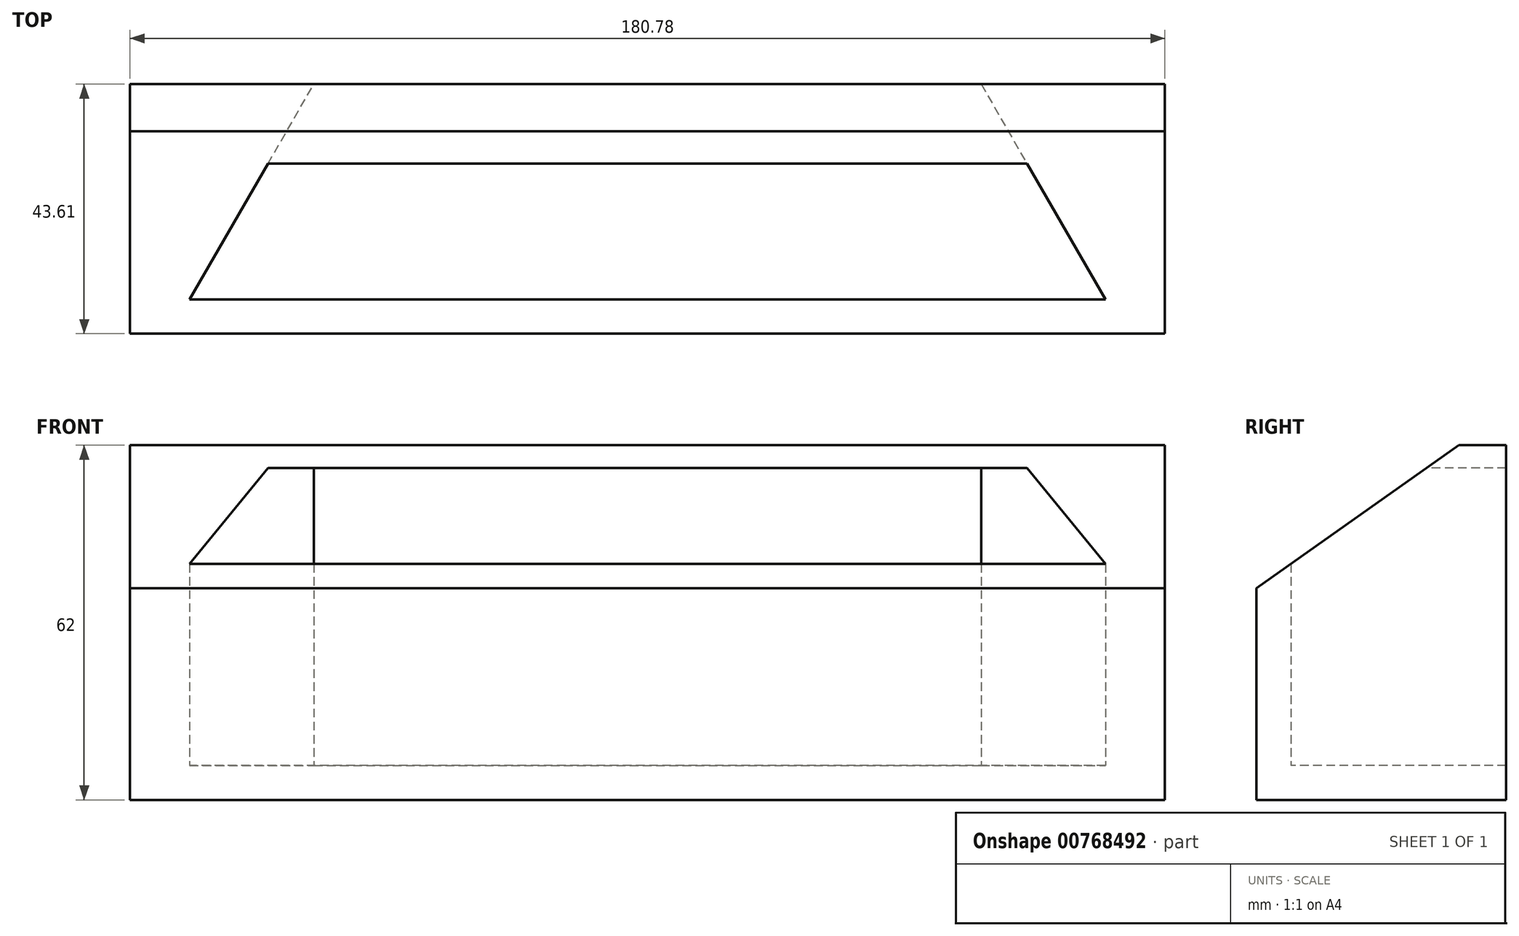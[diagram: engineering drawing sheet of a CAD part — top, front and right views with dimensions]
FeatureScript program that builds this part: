
annotation { "Feature Type Name" : "Feature", "Feature Type Description" : "" }
export const myFeature = defineFeature(function(context is Context, id is Id, definition is map)
    precondition{}
    {
        {
            var Q0;
            Q0=qCreatedBy(makeId("Top.planeOp"),FACE);
            var sketch = newSketch(context, id + "F0", { "sketchPlane" : qUnion([Q0])});
            skLineSegment(sketch, "E0.0", {"start": v(-80, -24) * mm, "end": v(0, 114.56) * mm});
            skLineSegment(sketch, "E0.1", {"start": v(0, 114.56) * mm, "end": v(80, -24) * mm});
            skLineSegment(sketch, "E0.2", {"start": v(80, -24) * mm, "end": v(-80, -24) * mm});
            skPoint(sketch, "E0.0.midPoint", {"position": v(-40, 45.28) * mm});
            skLineSegment(sketch, "E1", {"start": v(0, 126.56) * mm, "end": v(-90.4, -30) * mm});
            skLineSegment(sketch, "E2", {"start": v(-90.4, -30) * mm, "end": v(90.4, -30) * mm});
            skLineSegment(sketch, "E3", {"start": v(90.4, -30) * mm, "end": v(0, 126.56) * mm});
            skLineSegment(sketch, "E4", {"start": v(-90.4, -30) * mm, "end": v(-90.4, 0) * mm});
            skLineSegment(sketch, "E5", {"start": v(73.07, 0) * mm, "end": v(90.4, 0) * mm});
            skLineSegment(sketch, "E6", {"start": v(90.4, -30) * mm, "end": v(90.4, 0) * mm});
            skLineSegment(sketch, "E7", {"start": v(-90.4, 0) * mm, "end": v(-73.07, 0) * mm});
            skLineSegment(sketch, "E8", {"start": v(-58.29, 13.6) * mm, "end": v(58.29, 13.6) * mm});
            skLineSegment(sketch, "E9", {"start": v(-58.29, 13.6) * mm, "end": v(-65.21, 13.6) * mm});
            skLineSegment(sketch, "E10", {"start": v(58.29, 13.6) * mm, "end": v(65.21, 13.6) * mm});
            skLineSegment(sketch, "E11", {"start": v(-90.4, 0) * mm, "end": v(-90.4, 13.6) * mm});
            skLineSegment(sketch, "E12", {"start": v(-65.21, 13.6) * mm, "end": v(-90.4, 13.6) * mm});
            skLineSegment(sketch, "E13", {"start": v(90.4, 0) * mm, "end": v(90.4, 13.6) * mm});
            skLineSegment(sketch, "E14", {"start": v(65.21, 13.6) * mm, "end": v(90.4, 13.6) * mm});
            skLineSegment(sketch, "E15", {"start": v(-90.4, -30) * mm, "end": v(-90.4, -51.53) * mm});
            skLineSegment(sketch, "E16", {"start": v(-90.4, -51.53) * mm, "end": v(90.4, -51.53) * mm});
            skLineSegment(sketch, "E17", {"start": v(90.4, -30) * mm, "end": v(90.4, -51.53) * mm});
            skSolve(sketch);
        }
        {
            var Q0;
            {var subQ4=sQuery(id+"F0.wireOp",EDGE,"E0.2");Q0=makeQuery(id+"F0.imprint","IMPRINT",FACE,{"disambiguationData":[TD([[makeQuery(id+"F0.imprint","IMPRINT",EDGE,{"derivedFrom":subQ4}),1.0]])]});}
            var Q1;
            {var subQ0=sQuery(id+"F0.wireOp",EDGE,"E4");Q1=makeQuery(id+"F0.imprint","IMPRINT",FACE,{"disambiguationData":[TD([[makeQuery(id+"F0.imprint","IMPRINT",EDGE,{"derivedFrom":subQ0}),-1.0]])]});}
            var Q2;
            {var subQ0=sQuery(id+"F0.wireOp",EDGE,"E6");Q2=makeQuery(id+"F0.imprint","IMPRINT",FACE,{"disambiguationData":[TD([[makeQuery(id+"F0.imprint","IMPRINT",EDGE,{"derivedFrom":subQ0}),1.0]])]});}
            var Q3;
            {var subQ0=sQuery(id+"F0.wireOp",EDGE,"E7");Q3=makeQuery(id+"F0.imprint","IMPRINT",FACE,{"disambiguationData":[TD([[makeQuery(id+"F0.imprint","IMPRINT",EDGE,{"derivedFrom":subQ0}),1.0]])]});}
            var Q4;
            {var subQ0=sQuery(id+"F0.wireOp",EDGE,"E5");Q4=makeQuery(id+"F0.imprint","IMPRINT",FACE,{"disambiguationData":[TD([[makeQuery(id+"F0.imprint","IMPRINT",EDGE,{"derivedFrom":subQ0}),1.0]])]});}
            extrude(context, id + "F1", {"entities" : qUnion([Q0, Q1, Q2, Q3, Q4]), "depth" : 56 * mm, "offsetDistance" : 25 * mm});
        }
        {
            var Q0;
            Q0=makeQuery(id+"F1.opExtrude","CAP_EDGE",EDGE,{"disambiguationData":[OSD([sQuery(id+"F0.wireOp",EDGE,"E2")])],"isStart":false});
            chamfer(context, id + "F2", {"entities" : qUnion([Q0]), "chamferType" : ChamferType.OFFSET_ANGLE, "width" : 25 * mm, "oppositeDirection" : true, "angle" : 54.74 * degree, "tangentPropagation" : true});
        }
        {
            var Q0;
            {var subQ0=sQuery(id+"F0.wireOp",EDGE,"E0.2");Q0=makeQuery(id+"F0.imprint","IMPRINT",FACE,{"disambiguationData":[TD([[makeQuery(id+"F0.imprint","IMPRINT",EDGE,{"derivedFrom":subQ0}),-1.0]])]});}
            extrude(context, id + "F3", {"entities" : qUnion([Q0]), "operationType" : NewBodyOperationType.ADD, "depth" : 56 * mm, "offsetDistance" : 25 * mm});
        }
        {
            var Q0;
            Q0=makeQuery(id+"F2.opChamfer","BLEND_FACE",FACE,{"disambiguationData":[OSD([sQuery(id+"F0.wireOp",EDGE,"E2")])]});
            cPlane(context, id + "F4", {"entities" : qUnion([Q0]), "cplaneType" : CPlaneType.OFFSET, "offset" : 0 * mm, "width" : 150 * mm, "height" : 150 * mm});
        }
        {
            var Q0;
            Q0=qCreatedBy(id+"F4.planeOp",FACE);
            var sketch = newSketch(context, id + "F5", { "sketchPlane" : qUnion([Q0])});
            skLineSegment(sketch, "E18.bottom", {"start": v(-123.92, 59.92) * mm, "end": v(135.6, 59.92) * mm});
            skLineSegment(sketch, "E18.top", {"start": v(-123.92, -61.5) * mm, "end": v(135.6, -61.5) * mm});
            skLineSegment(sketch, "E18.left", {"start": v(-123.92, 59.92) * mm, "end": v(-123.92, -61.5) * mm});
            skLineSegment(sketch, "E18.right", {"start": v(135.6, 59.92) * mm, "end": v(135.6, -61.5) * mm});
            skSolve(sketch);
        }
        {
            var Q0;
            {var subQ0=sQuery(id+"F0.wireOp",EDGE,"E0.2");Q0=makeQuery(id+"F0.imprint","IMPRINT",FACE,{"disambiguationData":[TD([[makeQuery(id+"F0.imprint","IMPRINT",EDGE,{"derivedFrom":subQ0}),-1.0]])]});}
            var Q1;
            {var subQ3=sQuery(id+"F0.wireOp",EDGE,"E0.2");Q1=makeQuery(id+"F0.imprint","IMPRINT",FACE,{"disambiguationData":[TD([[makeQuery(id+"F0.imprint","IMPRINT",EDGE,{"derivedFrom":subQ3}),1.0]])]});}
            var Q2;
            {var subQ0=sQuery(id+"F0.wireOp",EDGE,"E4");Q2=makeQuery(id+"F0.imprint","IMPRINT",FACE,{"disambiguationData":[TD([[makeQuery(id+"F0.imprint","IMPRINT",EDGE,{"derivedFrom":subQ0}),-1.0]])]});}
            var Q3;
            {var subQ0=sQuery(id+"F0.wireOp",EDGE,"E7");Q3=makeQuery(id+"F0.imprint","IMPRINT",FACE,{"disambiguationData":[TD([[makeQuery(id+"F0.imprint","IMPRINT",EDGE,{"derivedFrom":subQ0}),1.0]])]});}
            var Q4;
            {var subQ0=sQuery(id+"F0.wireOp",EDGE,"E5");Q4=makeQuery(id+"F0.imprint","IMPRINT",FACE,{"disambiguationData":[TD([[makeQuery(id+"F0.imprint","IMPRINT",EDGE,{"derivedFrom":subQ0}),1.0]])]});}
            var Q5;
            {var subQ2=sQuery(id+"F0.wireOp",EDGE,"E5");Q5=makeQuery(id+"F0.imprint","IMPRINT",FACE,{"disambiguationData":[TD([[makeQuery(id+"F0.imprint","IMPRINT",EDGE,{"derivedFrom":subQ2}),-1.0]])]});}
            extrude(context, id + "F6", {"entities" : qUnion([Q0, Q1, Q2, Q3, Q4, Q5]), "operationType" : NewBodyOperationType.ADD, "oppositeDirection" : true, "depth" : 6 * mm, "offsetDistance" : 25 * mm});
        }
        {
            var Q0;
            Q0=makeQuery(id+"F5.imprint","IMPRINT",FACE,{"disambiguationData":[TD([[makeQuery(id+"F5.imprint","IMPRINT",EDGE,{"derivedFrom":sQuery(id+"F5.wireOp",EDGE,"E18.bottom")}),-1.0]])]});
            extrude(context, id + "F7", {"entities" : qUnion([Q0]), "operationType" : NewBodyOperationType.REMOVE, "depth" : 25 * mm, "offsetDistance" : 25 * mm});
        }
        {
            var Q0;
            {var subQ0=sQuery(id+"F0.wireOp",EDGE,"E0.2");Q0=makeQuery(id+"F0.imprint","IMPRINT",FACE,{"disambiguationData":[TD([[makeQuery(id+"F0.imprint","IMPRINT",EDGE,{"derivedFrom":subQ0}),-1.0]])]});}
            extrude(context, id + "F8", {"entities" : qUnion([Q0]), "operationType" : NewBodyOperationType.REMOVE, "depth" : 52 * mm, "offsetDistance" : 25 * mm});
        }
    });
